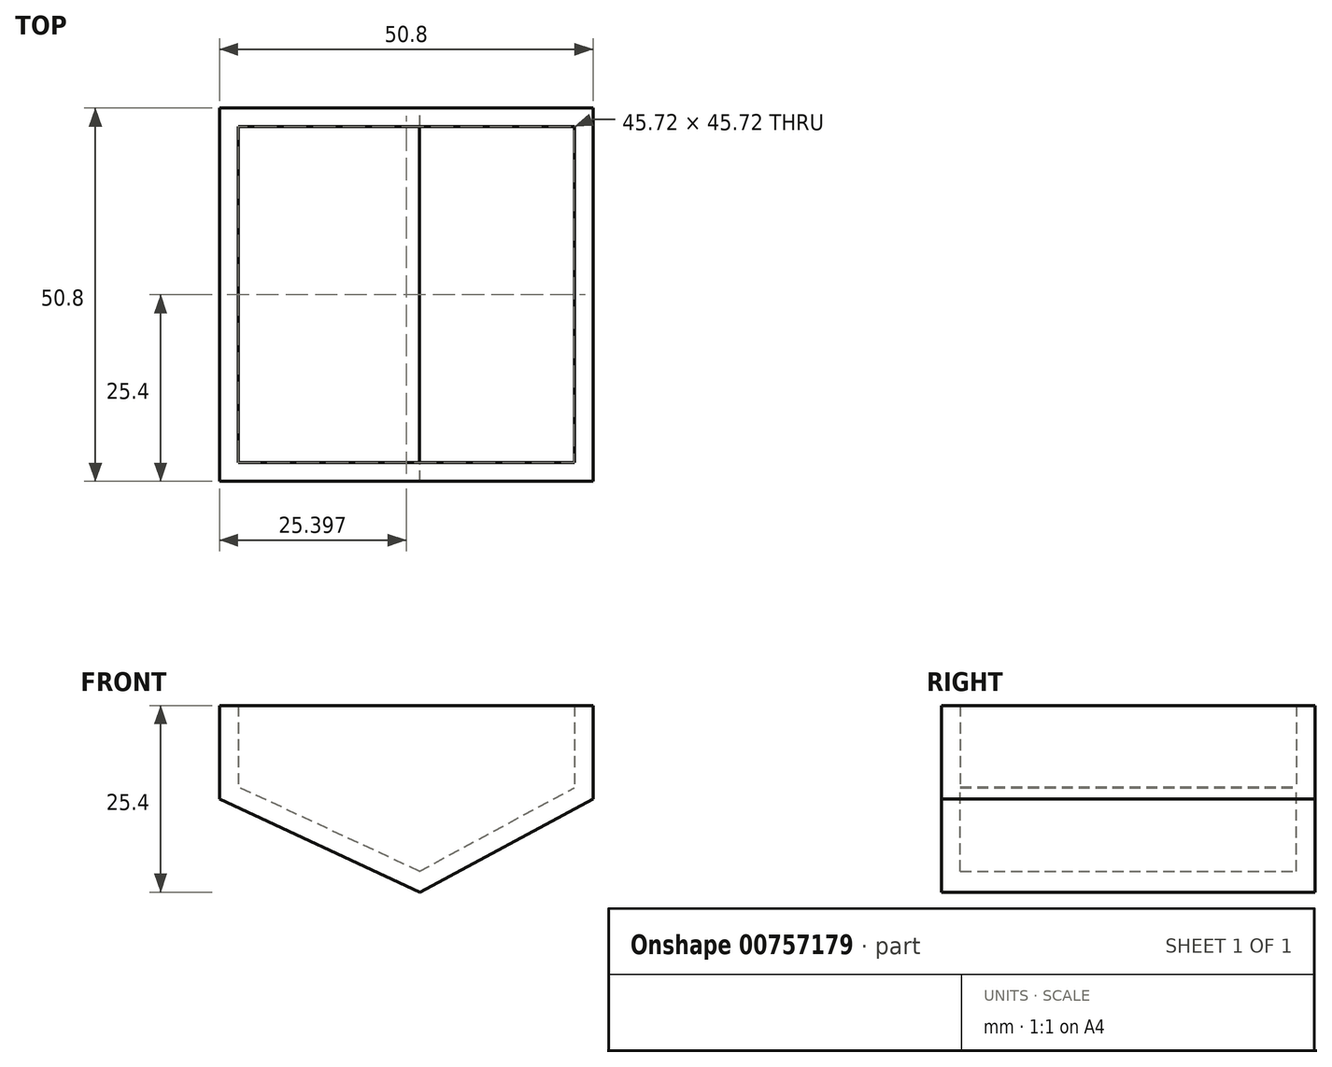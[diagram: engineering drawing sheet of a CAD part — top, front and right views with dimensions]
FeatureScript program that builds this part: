
annotation { "Feature Type Name" : "Feature", "Feature Type Description" : "" }
export const myFeature = defineFeature(function(context is Context, id is Id, definition is map)
    precondition{}
    {
        {
            var Q0;
            Q0=qCreatedBy(makeId("Front.planeOp"),FACE);
            var sketch = newSketch(context, id + "F0", { "sketchPlane" : qUnion([Q0])});
            skLineSegment(sketch, "E0", {"start": v(-27.3, 12.7) * mm, "end": v(23.5, 12.7) * mm});
            skLineSegment(sketch, "E1", {"start": v(23.5, 12.7) * mm, "end": v(23.5, 0) * mm});
            skLineSegment(sketch, "E2", {"start": v(-27.3, 12.7) * mm, "end": v(-27.3, 0) * mm});
            skLineSegment(sketch, "E3", {"start": v(0, 12.7) * mm, "end": v(0, -12.7) * mm});
            skLineSegment(sketch, "E4", {"start": v(0, -12.7) * mm, "end": v(-27.3, 0) * mm});
            skLineSegment(sketch, "E5", {"start": v(0, -12.7) * mm, "end": v(23.5, 0) * mm});
            skSolve(sketch);
        }
        {
            var Q0;
            {var subQ0=sQuery(id+"F0.wireOp",EDGE,"E1");Q0=makeQuery(id+"F0.imprint","IMPRINT",FACE,{"disambiguationData":[TD([[makeQuery(id+"F0.imprint","IMPRINT",EDGE,{"derivedFrom":subQ0}),-1.0]])]});}
            var Q1;
            {var subQ0=sQuery(id+"F0.wireOp",EDGE,"E2");Q1=makeQuery(id+"F0.imprint","IMPRINT",FACE,{"disambiguationData":[TD([[makeQuery(id+"F0.imprint","IMPRINT",EDGE,{"derivedFrom":subQ0}),1.0]])]});}
            extrude(context, id + "F1", {"entities" : qUnion([Q0, Q1]), "depth" : 50.8 * mm, "offsetDistance" : 25.4 * mm});
        }
        {
            var Q0;
            Q0=makeQuery(id+"F1.opExtrude","SWEPT_FACE",FACE,{"disambiguationData":[OSD([sQuery(id+"F0.wireOp",EDGE,"E0")])]});
            shell(context, id + "F2", {"entities" : qUnion([Q0]), "thickness" : 2.54 * mm});
        }
    });
